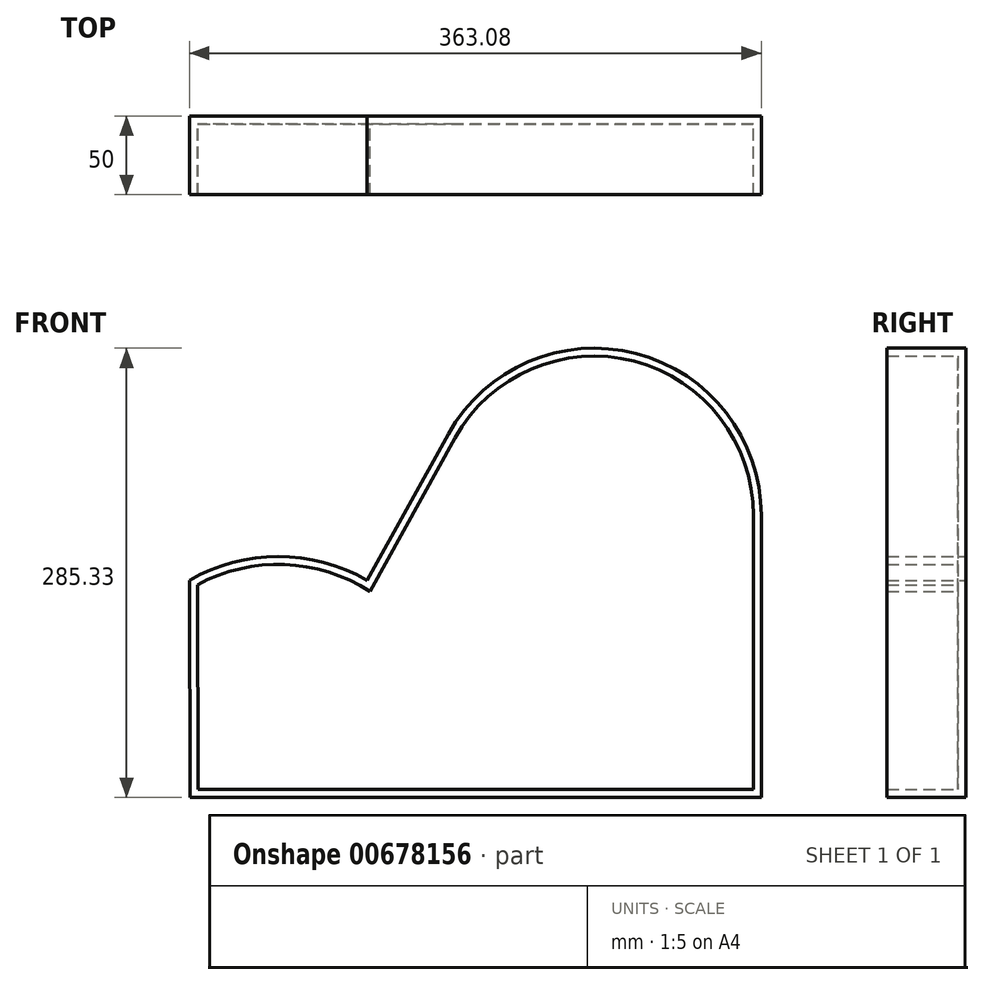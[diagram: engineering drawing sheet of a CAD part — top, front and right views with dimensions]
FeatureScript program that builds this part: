
annotation { "Feature Type Name" : "Feature", "Feature Type Description" : "" }
export const myFeature = defineFeature(function(context is Context, id is Id, definition is map)
    precondition{}
    {
        {
            var Q0;
            Q0=qCreatedBy(makeId("Front.planeOp"),FACE);
            var sketch = newSketch(context, id + "F0", { "sketchPlane" : qUnion([Q0])});
            skCircle(sketch, "E0", {"center": v(0, 0) * mm, "radius": 53.72 * mm});
            skCircle(sketch, "E1", {"center": v(0, 0) * mm, "radius": 58.67 * mm, "construction": true});
            skCircle(sketch, "E2", {"center": v(0, 0) * mm, "radius": 63.5 * mm, "construction": true});
            skLineSegment(sketch, "E3", {"start": v(0, 0) * mm, "end": v(0, 76.94) * mm, "construction": true});
            skLineSegment(sketch, "E4", {"start": v(0, 0) * mm, "end": v(-5.87, 89.51) * mm, "construction": true});
            skLineSegment(sketch, "E5", {"start": v(0, 58.67) * mm, "end": v(-67.61, 58.67) * mm, "construction": true});
            skLineSegment(sketch, "E6", {"start": v(0, 58.67) * mm, "end": v(-66.6, 34.44) * mm, "construction": true});
            skCircle(sketch, "E7", {"center": v(0, 0) * mm, "radius": 55.14 * mm, "construction": true});
            skCircle(sketch, "E8", {"center": v(0, 58.67) * mm, "radius": 14.6 * mm, "construction": true});
            skCircle(sketch, "E9", {"center": v(-13.72, 53.68) * mm, "radius": 14.6 * mm, "construction": true});
            skArc(sketch, "E10", {"start": v(0, 58.67) * mm, "mid": v(-1.2, 61.2) * mm, "end": v(-2.86, 63.44) * mm});
            skArc(sketch, "E11", {"start": v(0.88, 53.71) * mm, "mid": v(0.65, 56.23) * mm, "end": v(0, 58.67) * mm});
            skArc(sketch, "E12.MirrorCS", {"start": v(-7.66, 58.17) * mm, "mid": v(-6.8, 60.83) * mm, "end": v(-5.45, 63.27) * mm});
            skArc(sketch, "E13.MirrorCS", {"start": v(-7.88, 53.14) * mm, "mid": v(-7.98, 55.67) * mm, "end": v(-7.66, 58.17) * mm});
            skArc(sketch, "E14", {"start": v(-2.86, 63.44) * mm, "mid": v(-4.16, 63.52) * mm, "end": v(-5.45, 63.27) * mm});
            skCircle(sketch, "E15.cCircle", {"center": v(0, 0) * mm, "radius": 11.38 * mm, "construction": true});
            skLineSegment(sketch, "E15.0", {"start": v(-6.57, 11.38) * mm, "end": v(6.57, 11.38) * mm});
            skLineSegment(sketch, "E15.1", {"start": v(6.57, 11.38) * mm, "end": v(13.14, 0) * mm});
            skLineSegment(sketch, "E15.2", {"start": v(13.14, 0) * mm, "end": v(6.57, -11.38) * mm});
            skLineSegment(sketch, "E15.3", {"start": v(6.57, -11.38) * mm, "end": v(-6.57, -11.38) * mm});
            skLineSegment(sketch, "E15.4", {"start": v(-6.57, -11.38) * mm, "end": v(-13.14, 0) * mm});
            skLineSegment(sketch, "E15.5", {"start": v(-13.14, 0) * mm, "end": v(-6.57, 11.38) * mm});
            skPoint(sketch, "E15.0.midPoint", {"position": v(0, 11.38) * mm});
            skLineSegment(sketch, "E16.bottom", {"start": v(-27.76, 28.86) * mm, "end": v(27.76, 28.86) * mm});
            skLineSegment(sketch, "E16.top", {"start": v(-27.76, -28.86) * mm, "end": v(27.76, -28.86) * mm});
            skLineSegment(sketch, "E16.left", {"start": v(-27.76, 28.86) * mm, "end": v(-27.76, -28.86) * mm});
            skLineSegment(sketch, "E16.right", {"start": v(27.76, 28.86) * mm, "end": v(27.76, -28.86) * mm});
            skSolve(sketch);
        }
        {
            var Q0;
            {var subQ0=sQuery(id+"F0.wireOp",EDGE,"E0");var subQ1=makeQuery(id+"F0.imprint","INTERSECT",VERTEX,{"derivedFrom":[subQ0,sQuery(id+"F0.wireOp",EDGE,"E11")]});Q0=makeQuery(id+"F0.imprint","IMPRINT",FACE,{"disambiguationData":[TD([[makeQuery(id+"F0.imprint","IMPRINT",EDGE,{"disambiguationData":[TD([[subQ1,-1.0]])],"derivedFrom":subQ0}),1.0]])]});}
            var Q1;
            Q1=makeQuery(id+"F0.imprint","IMPRINT",FACE,{"disambiguationData":[TD([[makeQuery(id+"F0.imprint","IMPRINT",EDGE,{"derivedFrom":sQuery(id+"F0.wireOp",EDGE,"E10")}),1.0]])]});
            extrude(context, id + "F1", {"entities" : qUnion([Q0, Q1]), "depth" : 25 * mm, "offsetDistance" : 25 * mm});
        }
        {
            var Q0;
            Q0=makeQuery(id+"F1.opExtrude","SWEPT_BODY",BODY,{"disambiguationData":[OSD([sQuery(id+"F0.wireOp",EDGE,"E0"),sQuery(id+"F0.wireOp",EDGE,"E10"),sQuery(id+"F0.wireOp",EDGE,"E11"),sQuery(id+"F0.wireOp",EDGE,"E12.MirrorCS"),sQuery(id+"F0.wireOp",EDGE,"E13.MirrorCS"),sQuery(id+"F0.wireOp",EDGE,"E14")])]});
            var Q1;
            Q1=makeQuery(id+"F1.opExtrude","SWEPT_FACE",FACE,{"disambiguationData":[OSD([sQuery(id+"F0.wireOp",EDGE,"E0")])]});
            circularPattern(context, id + "F2", {"entities" : qUnion([Q0]), "axis" : qUnion([Q1]), "angle" : 360 * degree, "instanceCount" : 24, "equalSpace" : true});
        }
        {
            var Q0;
            Q0=makeQuery(id+"F0.imprint","IMPRINT",FACE,{"disambiguationData":[TD([[makeQuery(id+"F0.imprint","IMPRINT",EDGE,{"derivedFrom":sQuery(id+"F0.wireOp",EDGE,"E15.0")}),1.0]])]});
            extrude(context, id + "F3", {"entities" : qUnion([Q0]), "operationType" : NewBodyOperationType.ADD, "depth" : 35 * mm, "offsetDistance" : 25 * mm});
        }
        {
            var Q0;
            {var subQ0=makeQuery(id+"F1.opExtrude","CAP_FACE",FACE,{"disambiguationData":[OSD([sQuery(id+"F0.wireOp",EDGE,"E0"),sQuery(id+"F0.wireOp",EDGE,"E10"),sQuery(id+"F0.wireOp",EDGE,"E11"),sQuery(id+"F0.wireOp",EDGE,"E12.MirrorCS"),sQuery(id+"F0.wireOp",EDGE,"E13.MirrorCS"),sQuery(id+"F0.wireOp",EDGE,"E14"),sQuery(id+"F0.wireOp",EDGE,"E16.bottom"),sQuery(id+"F0.wireOp",EDGE,"E16.top"),sQuery(id+"F0.wireOp",EDGE,"E16.left"),sQuery(id+"F0.wireOp",EDGE,"E16.right")])],"isStart":false});Q0=makeQuery(id+"F3.boolean.opBoolean","MERGE",FACE,{"derivedFrom":[subQ0,makeQuery(id+"F2.opPattern","COPY",FACE,{"derivedFrom":subQ0,"instanceName":"1"}),makeQuery(id+"F2.opPattern","COPY",FACE,{"derivedFrom":subQ0,"instanceName":"2"}),makeQuery(id+"F2.opPattern","COPY",FACE,{"derivedFrom":subQ0,"instanceName":"3"}),makeQuery(id+"F2.opPattern","COPY",FACE,{"derivedFrom":subQ0,"instanceName":"4"}),makeQuery(id+"F2.opPattern","COPY",FACE,{"derivedFrom":subQ0,"instanceName":"5"}),makeQuery(id+"F2.opPattern","COPY",FACE,{"derivedFrom":subQ0,"instanceName":"6"}),makeQuery(id+"F2.opPattern","COPY",FACE,{"derivedFrom":subQ0,"instanceName":"7"}),makeQuery(id+"F2.opPattern","COPY",FACE,{"derivedFrom":subQ0,"instanceName":"8"}),makeQuery(id+"F2.opPattern","COPY",FACE,{"derivedFrom":subQ0,"instanceName":"9"}),makeQuery(id+"F2.opPattern","COPY",FACE,{"derivedFrom":subQ0,"instanceName":"10"}),makeQuery(id+"F2.opPattern","COPY",FACE,{"derivedFrom":subQ0,"instanceName":"11"}),makeQuery(id+"F2.opPattern","COPY",FACE,{"derivedFrom":subQ0,"instanceName":"12"}),makeQuery(id+"F2.opPattern","COPY",FACE,{"derivedFrom":subQ0,"instanceName":"13"}),makeQuery(id+"F2.opPattern","COPY",FACE,{"derivedFrom":subQ0,"instanceName":"14"}),makeQuery(id+"F2.opPattern","COPY",FACE,{"derivedFrom":subQ0,"instanceName":"15"}),makeQuery(id+"F2.opPattern","COPY",FACE,{"derivedFrom":subQ0,"instanceName":"16"}),makeQuery(id+"F2.opPattern","COPY",FACE,{"derivedFrom":subQ0,"instanceName":"17"}),makeQuery(id+"F2.opPattern","COPY",FACE,{"derivedFrom":subQ0,"instanceName":"18"}),makeQuery(id+"F2.opPattern","COPY",FACE,{"derivedFrom":subQ0,"instanceName":"19"}),makeQuery(id+"F2.opPattern","COPY",FACE,{"derivedFrom":subQ0,"instanceName":"20"}),makeQuery(id+"F2.opPattern","COPY",FACE,{"derivedFrom":subQ0,"instanceName":"21"}),makeQuery(id+"F2.opPattern","COPY",FACE,{"derivedFrom":subQ0,"instanceName":"22"}),makeQuery(id+"F2.opPattern","COPY",FACE,{"derivedFrom":subQ0,"instanceName":"23"})]});}
            var Q1;
            {var subQ0=sQuery(id+"F0.wireOp",EDGE,"E16.right");var subQ1=sQuery(id+"F0.wireOp",EDGE,"E16.left");var subQ2=sQuery(id+"F0.wireOp",EDGE,"E16.top");var subQ3=sQuery(id+"F0.wireOp",EDGE,"E16.bottom");var subQ4=makeQuery(id+"F1.opExtrude","CAP_FACE",FACE,{"disambiguationData":[OSD([sQuery(id+"F0.wireOp",EDGE,"E0"),sQuery(id+"F0.wireOp",EDGE,"E10"),sQuery(id+"F0.wireOp",EDGE,"E11"),sQuery(id+"F0.wireOp",EDGE,"E12.MirrorCS"),sQuery(id+"F0.wireOp",EDGE,"E13.MirrorCS"),sQuery(id+"F0.wireOp",EDGE,"E14"),subQ3,subQ2,subQ1,subQ0])],"isStart":true});Q1=makeQuery(id+"F3.boolean.opBoolean","MERGE",FACE,{"derivedFrom":[subQ4,makeQuery(id+"F2.opPattern","COPY",FACE,{"derivedFrom":subQ4,"instanceName":"1"}),makeQuery(id+"F2.opPattern","COPY",FACE,{"derivedFrom":subQ4,"instanceName":"2"}),makeQuery(id+"F2.opPattern","COPY",FACE,{"derivedFrom":subQ4,"instanceName":"3"}),makeQuery(id+"F2.opPattern","COPY",FACE,{"derivedFrom":subQ4,"instanceName":"4"}),makeQuery(id+"F2.opPattern","COPY",FACE,{"derivedFrom":subQ4,"instanceName":"5"}),makeQuery(id+"F2.opPattern","COPY",FACE,{"derivedFrom":subQ4,"instanceName":"6"}),makeQuery(id+"F2.opPattern","COPY",FACE,{"derivedFrom":subQ4,"instanceName":"7"}),makeQuery(id+"F2.opPattern","COPY",FACE,{"derivedFrom":subQ4,"instanceName":"8"}),makeQuery(id+"F2.opPattern","COPY",FACE,{"derivedFrom":subQ4,"instanceName":"9"}),makeQuery(id+"F2.opPattern","COPY",FACE,{"derivedFrom":subQ4,"instanceName":"10"}),makeQuery(id+"F2.opPattern","COPY",FACE,{"derivedFrom":subQ4,"instanceName":"11"}),makeQuery(id+"F2.opPattern","COPY",FACE,{"derivedFrom":subQ4,"instanceName":"12"}),makeQuery(id+"F2.opPattern","COPY",FACE,{"derivedFrom":subQ4,"instanceName":"13"}),makeQuery(id+"F2.opPattern","COPY",FACE,{"derivedFrom":subQ4,"instanceName":"14"}),makeQuery(id+"F2.opPattern","COPY",FACE,{"derivedFrom":subQ4,"instanceName":"15"}),makeQuery(id+"F2.opPattern","COPY",FACE,{"derivedFrom":subQ4,"instanceName":"16"}),makeQuery(id+"F2.opPattern","COPY",FACE,{"derivedFrom":subQ4,"instanceName":"17"}),makeQuery(id+"F2.opPattern","COPY",FACE,{"derivedFrom":subQ4,"instanceName":"18"}),makeQuery(id+"F2.opPattern","COPY",FACE,{"derivedFrom":subQ4,"instanceName":"19"}),makeQuery(id+"F2.opPattern","COPY",FACE,{"derivedFrom":subQ4,"instanceName":"20"}),makeQuery(id+"F2.opPattern","COPY",FACE,{"derivedFrom":subQ4,"instanceName":"21"}),makeQuery(id+"F2.opPattern","COPY",FACE,{"derivedFrom":subQ4,"instanceName":"22"}),makeQuery(id+"F2.opPattern","COPY",FACE,{"derivedFrom":subQ4,"instanceName":"23"}),makeQuery(id+"F3.opExtrude","CAP_FACE",FACE,{"disambiguationData":[OSD([sQuery(id+"F0.wireOp",EDGE,"E15.0"),sQuery(id+"F0.wireOp",EDGE,"E15.1"),sQuery(id+"F0.wireOp",EDGE,"E15.2"),sQuery(id+"F0.wireOp",EDGE,"E15.3"),sQuery(id+"F0.wireOp",EDGE,"E15.4"),sQuery(id+"F0.wireOp",EDGE,"E15.5"),subQ3,subQ2,subQ1,subQ0])],"isStart":true})]});}
            chamfer(context, id + "F4", {"entities" : qUnion([Q0, Q1]), "width" : 1 * mm, "tangentPropagation" : true});
        }
        {
            var Q0;
            Q0=makeQuery(id+"F3.opExtrude","CAP_FACE",FACE,{"disambiguationData":[OSD([sQuery(id+"F0.wireOp",EDGE,"E15.0"),sQuery(id+"F0.wireOp",EDGE,"E15.1"),sQuery(id+"F0.wireOp",EDGE,"E15.2"),sQuery(id+"F0.wireOp",EDGE,"E15.3"),sQuery(id+"F0.wireOp",EDGE,"E15.4"),sQuery(id+"F0.wireOp",EDGE,"E15.5"),sQuery(id+"F0.wireOp",EDGE,"E16.bottom"),sQuery(id+"F0.wireOp",EDGE,"E16.top"),sQuery(id+"F0.wireOp",EDGE,"E16.left"),sQuery(id+"F0.wireOp",EDGE,"E16.right")])],"isStart":false});
            var Q1;
            Q1=makeQuery(id+"F3.opExtrude","SWEPT_FACE",FACE,{"disambiguationData":[OSD([sQuery(id+"F0.wireOp",EDGE,"E16.left")])]});
            var Q2;
            Q2=makeQuery(id+"F3.opExtrude","SWEPT_FACE",FACE,{"disambiguationData":[OSD([sQuery(id+"F0.wireOp",EDGE,"E16.right")])]});
            var Q3;
            Q3=makeQuery(id+"F3.opExtrude","SWEPT_FACE",FACE,{"disambiguationData":[OSD([sQuery(id+"F0.wireOp",EDGE,"E16.bottom")])]});
            var Q4;
            Q4=makeQuery(id+"F3.opExtrude","SWEPT_FACE",FACE,{"disambiguationData":[OSD([sQuery(id+"F0.wireOp",EDGE,"E16.top")])]});
            fillet(context, id + "F5", {"entities" : qUnion([Q0, Q1, Q2, Q3, Q4]), "radius" : 1 * mm, "tangentPropagation" : true, "allowEdgeOverflow" : false});
        }
        {
            var Q0;
            Q0=qCreatedBy(makeId("Front.planeOp"),FACE);
            var sketch = newSketch(context, id + "F6", { "sketchPlane" : qUnion([Q0])});
            skLineSegment(sketch, "E17", {"start": v(-74.14, -74.16) * mm, "end": v(288.46, -74.16) * mm});
            skLineSegment(sketch, "E18", {"start": v(288.46, -74.16) * mm, "end": v(288.46, 105.1) * mm});
            skArc(sketch, "E19", {"start": v(288.46, 105.1) * mm, "mid": v(209.03, 207.77) * mm, "end": v(89.71, 156.67) * mm});
            skLineSegment(sketch, "E20", {"start": v(89.71, 156.67) * mm, "end": v(38.06, 63.83) * mm});
            skArc(sketch, "E21", {"start": v(38.06, 63.83) * mm, "mid": v(-18.28, 78.88) * mm, "end": v(-74.62, 63.83) * mm});
            skLineSegment(sketch, "E22", {"start": v(-74.62, 63.83) * mm, "end": v(-74.14, -74.16) * mm});
            skSolve(sketch);
        }
        {
            var Q0;
            Q0=makeQuery(id+"F6.imprint","IMPRINT",FACE,{"disambiguationData":[TD([[makeQuery(id+"F6.imprint","IMPRINT",EDGE,{"derivedFrom":sQuery(id+"F6.wireOp",EDGE,"E17")}),1.0]])]});
            extrude(context, id + "F7", {"entities" : qUnion([Q0]), "depth" : 50 * mm, "offsetDistance" : 25 * mm});
        }
        {
            var Q0;
            Q0=makeQuery(id+"F7.opExtrude","CAP_FACE",FACE,{"disambiguationData":[OSD([sQuery(id+"F6.wireOp",EDGE,"E17"),sQuery(id+"F6.wireOp",EDGE,"E18"),sQuery(id+"F6.wireOp",EDGE,"E19"),sQuery(id+"F6.wireOp",EDGE,"E20"),sQuery(id+"F6.wireOp",EDGE,"E21"),sQuery(id+"F6.wireOp",EDGE,"E22")])],"isStart":false});
            shell(context, id + "F8", {"entities" : qUnion([Q0]), "thickness" : 5 * mm});
        }
        {
            var Q0;
            Q0=makeQuery(id+"F1.opExtrude","SWEPT_BODY",BODY,{"disambiguationData":[OSD([sQuery(id+"F0.wireOp",EDGE,"E0"),sQuery(id+"F0.wireOp",EDGE,"E10"),sQuery(id+"F0.wireOp",EDGE,"E11"),sQuery(id+"F0.wireOp",EDGE,"E12.MirrorCS"),sQuery(id+"F0.wireOp",EDGE,"E13.MirrorCS"),sQuery(id+"F0.wireOp",EDGE,"E14"),sQuery(id+"F0.wireOp",EDGE,"E16.bottom"),sQuery(id+"F0.wireOp",EDGE,"E16.top"),sQuery(id+"F0.wireOp",EDGE,"E16.left"),sQuery(id+"F0.wireOp",EDGE,"E16.right")])]});
            deleteBodies(context, id + "F9", {"entities" : qUnion([Q0])});
        }
    });
